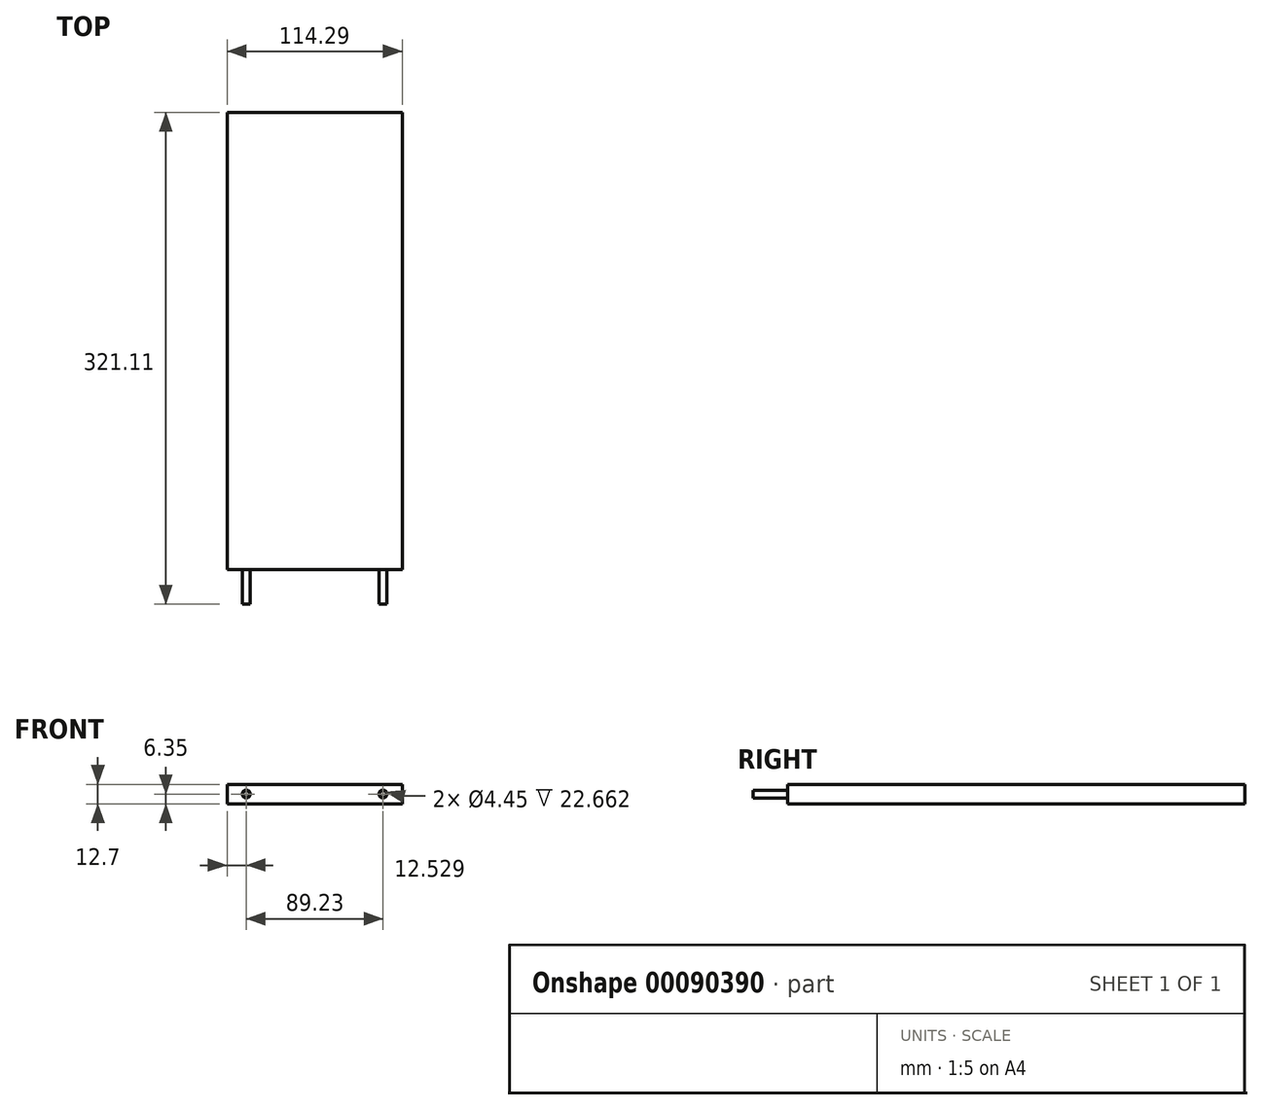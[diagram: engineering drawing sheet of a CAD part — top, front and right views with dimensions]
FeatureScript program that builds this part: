
annotation { "Feature Type Name" : "Feature", "Feature Type Description" : "" }
export const myFeature = defineFeature(function(context is Context, id is Id, definition is map)
    precondition{}
    {
        {
            var Q0;
            Q0=qCreatedBy(makeId("Top.planeOp"),FACE);
            var sketch = newSketch(context, id + "F0", { "sketchPlane" : qUnion([Q0])});
            skArc(sketch, "E0", {"start": v(-97.09, 52.34) * mm, "mid": v(-103.53, 58.69) * mm, "end": v(-109.78, 52.14) * mm});
            skArc(sketch, "E1", {"start": v(-71.69, 52.34) * mm, "mid": v(-78.04, 58.69) * mm, "end": v(-84.39, 52.34) * mm});
            skArc(sketch, "E2", {"start": v(-97.08, -201.86) * mm, "mid": v(-90.64, -208.01) * mm, "end": v(-84.39, -201.66) * mm});
            skArc(sketch, "E3", {"start": v(-71.69, -201.66) * mm, "mid": v(-65.34, -208.01) * mm, "end": v(-58.99, -201.66) * mm});
            skLineSegment(sketch, "E4", {"start": v(-84.39, -201.66) * mm, "end": v(-84.39, 52.34) * mm});
            skLineSegment(sketch, "E5", {"start": v(-71.69, 52.34) * mm, "end": v(-71.69, -201.66) * mm});
            skLineSegment(sketch, "E6", {"start": v(-58.99, -201.66) * mm, "end": v(-58.99, 52.37) * mm});
            skLineSegment(sketch, "E7", {"start": v(-33.59, -201.66) * mm, "end": v(-33.59, 52.47) * mm});
            skLineSegment(sketch, "E8", {"start": v(-109.78, 52.14) * mm, "end": v(-109.78, -252.6) * mm});
            skLineSegment(sketch, "E9", {"start": v(-20.89, 52.47) * mm, "end": v(-20.89, -252.6) * mm});
            skLineSegment(sketch, "E10", {"start": v(-97.08, -201.86) * mm, "end": v(-97.09, 52.34) * mm});
            skArc(sketch, "E11", {"start": v(-46.29, -201.66) * mm, "mid": v(-39.94, -208.01) * mm, "end": v(-33.59, -201.66) * mm});
            skArc(sketch, "E12", {"start": v(-46.3, 52.62) * mm, "mid": v(-52.76, 58.97) * mm, "end": v(-58.99, 52.37) * mm});
            skLineSegment(sketch, "E13", {"start": v(-46.3, 52.62) * mm, "end": v(-46.29, -201.66) * mm});
            skArc(sketch, "E14", {"start": v(-33.59, 52.47) * mm, "mid": v(-27.24, 58.82) * mm, "end": v(-20.89, 52.47) * mm});
            skSolve(sketch);
        }
        {
            var Q0;
            Q0=sQuery(id+"F0.wireOp",VERTEX,"E8.end");
            var Q1;
            Q1=qCreatedBy(makeId("Front.planeOp"),FACE);
            cPlane(context, id + "F1", {"entities" : qUnion([Q0, Q1]), "cplaneType" : CPlaneType.PLANE_POINT, "offset" : 152.4 * mm, "width" : 152.4 * mm, "height" : 152.4 * mm});
        }
        {
            var Q0;
            Q0=qCreatedBy(id+"F1.planeOp",FACE);
            var sketch = newSketch(context, id + "F2", { "sketchPlane" : qUnion([Q0])});
            skCircle(sketch, "E15", {"center": v(-109.95, 0) * mm, "radius": 2.54 * mm});
            skCircle(sketch, "E16", {"center": v(-109.95, 0) * mm, "radius": 2.22 * mm});
            skSolve(sketch);
        }
        {
            var Q0;
            Q0=makeQuery(id+"F2.imprint","IMPRINT",FACE,{"disambiguationData":[TD([[makeQuery(id+"F2.imprint","IMPRINT",EDGE,{"derivedFrom":sQuery(id+"F2.wireOp",EDGE,"E15")}),1.0]])]});
            var Q1;
            Q1=sQuery(id+"F0.wireOp",EDGE,"E8");
            var Q2;
            Q2=sQuery(id+"F0.wireOp",EDGE,"E0");
            var Q3;
            Q3=sQuery(id+"F0.wireOp",EDGE,"E10");
            var Q4;
            Q4=sQuery(id+"F0.wireOp",EDGE,"E2");
            var Q5;
            Q5=sQuery(id+"F0.wireOp",EDGE,"E4");
            var Q6;
            Q6=sQuery(id+"F0.wireOp",EDGE,"E1");
            var Q7;
            Q7=sQuery(id+"F0.wireOp",EDGE,"E5");
            var Q8;
            Q8=sQuery(id+"F0.wireOp",EDGE,"E3");
            var Q9;
            Q9=sQuery(id+"F0.wireOp",EDGE,"E6");
            var Q10;
            Q10=sQuery(id+"F0.wireOp",EDGE,"E12");
            var Q11;
            Q11=sQuery(id+"F0.wireOp",EDGE,"E13");
            var Q12;
            Q12=sQuery(id+"F0.wireOp",EDGE,"E11");
            var Q13;
            Q13=sQuery(id+"F0.wireOp",EDGE,"E7");
            var Q14;
            Q14=sQuery(id+"F0.wireOp",EDGE,"E14");
            var Q15;
            Q15=sQuery(id+"F0.wireOp",EDGE,"E9");
            sweep(context, id + "F3", {"profiles" : qUnion([Q0]), "path" : qUnion([Q1, Q2, Q3, Q4, Q5, Q6, Q7, Q8, Q9, Q10, Q11, Q12, Q13, Q14, Q15])});
        }
        {
            var Q0;
            Q0=qCreatedBy(makeId("Top.planeOp"),FACE);
            cPlane(context, id + "F4", {"entities" : qUnion([Q0]), "cplaneType" : CPlaneType.OFFSET, "offset" : 6.35 * mm, "width" : 152.4 * mm, "height" : 152.4 * mm});
        }
        {
            var Q0;
            Q0=qCreatedBy(id+"F4.planeOp",FACE);
            var sketch = newSketch(context, id + "F5", { "sketchPlane" : qUnion([Q0])});
            skLineSegment(sketch, "E17.bottom", {"start": v(-122.48, -229.94) * mm, "end": v(-8.19, -229.94) * mm});
            skLineSegment(sketch, "E17.top", {"start": v(-122.48, 68.5) * mm, "end": v(-8.19, 68.5) * mm});
            skLineSegment(sketch, "E17.left", {"start": v(-122.48, -229.94) * mm, "end": v(-122.48, 68.5) * mm});
            skLineSegment(sketch, "E17.right", {"start": v(-8.19, -229.94) * mm, "end": v(-8.19, 68.5) * mm});
            skSolve(sketch);
        }
        {
            var Q0;
            Q0 = qSketchRegion(id + "F5", true);
            extrude(context, id + "F6", {"entities" : qUnion([Q0]), "operationType" : NewBodyOperationType.ADD, "oppositeDirection" : true, "depth" : 12.7 * mm});
        }
    });
